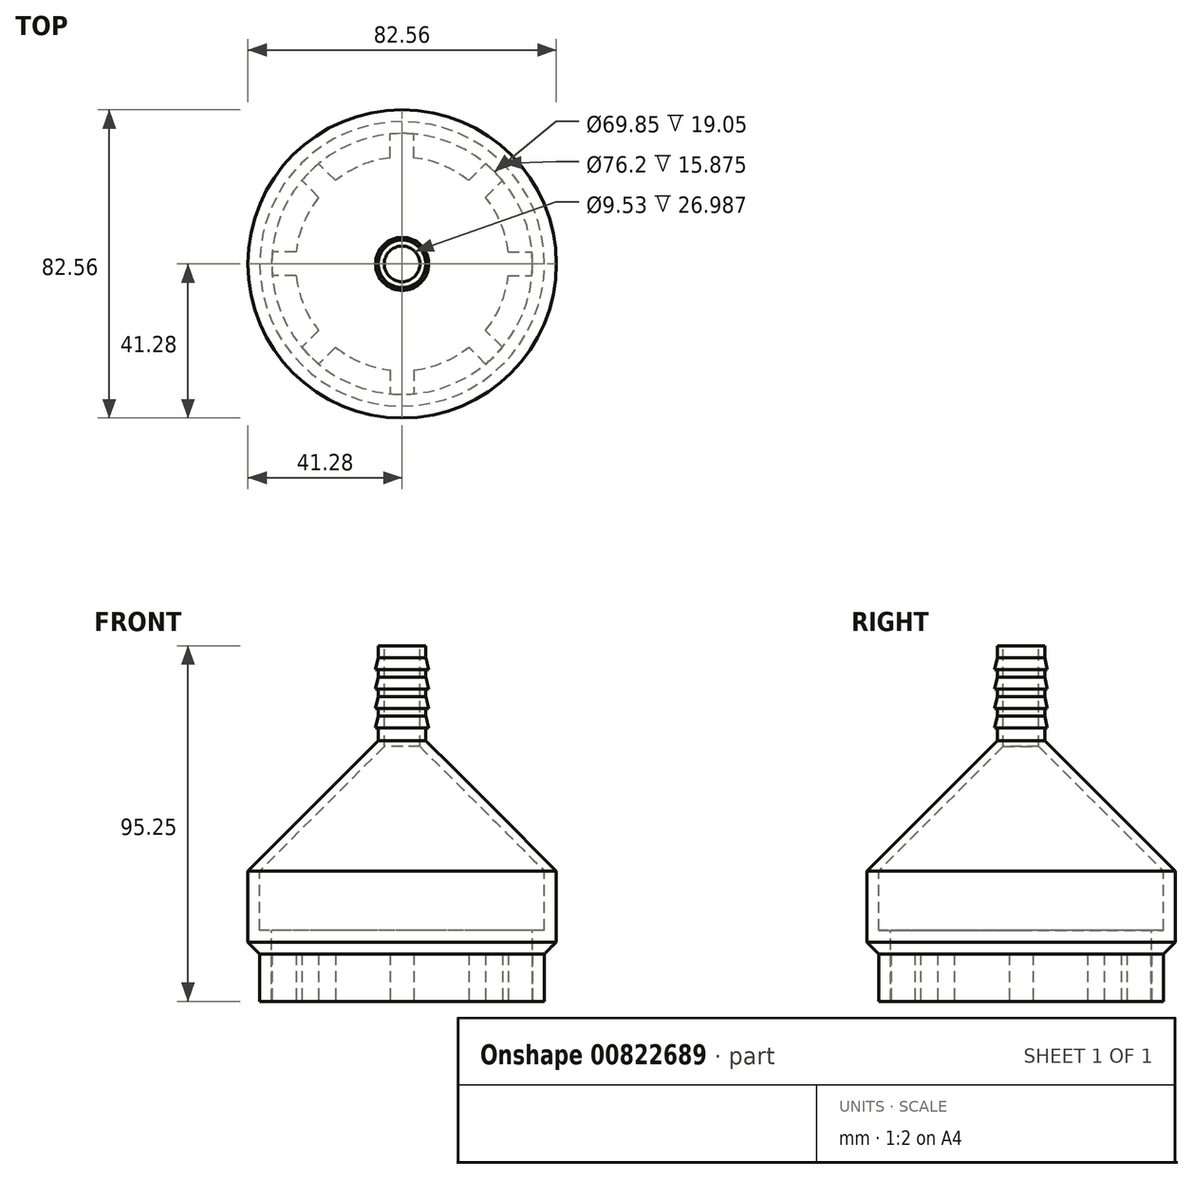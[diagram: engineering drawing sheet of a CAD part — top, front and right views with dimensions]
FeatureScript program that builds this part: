
annotation { "Feature Type Name" : "Feature", "Feature Type Description" : "" }
export const myFeature = defineFeature(function(context is Context, id is Id, definition is map)
    precondition{}
    {
        {
            var Q0;
            Q0=qCreatedBy(makeId("Front.planeOp"),FACE);
            var sketch = newSketch(context, id + "F0", { "sketchPlane" : qUnion([Q0])});
            skLineSegment(sketch, "E0", {"start": v(0, 0) * mm, "end": v(0, 101.6) * mm});
            skLineSegment(sketch, "E1", {"start": v(-34.93, 0) * mm, "end": v(0, 0) * mm});
            skLineSegment(sketch, "E2", {"start": v(-34.93, 0) * mm, "end": v(-38.1, 0) * mm});
            skLineSegment(sketch, "E3", {"start": v(-38.1, 0) * mm, "end": v(-38.1, 12.7) * mm});
            skLineSegment(sketch, "E4", {"start": v(-38.1, 12.7) * mm, "end": v(-41.27, 15.87) * mm});
            skLineSegment(sketch, "E5", {"start": v(-41.27, 15.87) * mm, "end": v(-41.27, 34.92) * mm});
            skLineSegment(sketch, "E6", {"start": v(-41.27, 34.92) * mm, "end": v(-6.35, 69.85) * mm});
            skLineSegment(sketch, "E7", {"start": v(-34.93, 0) * mm, "end": v(-34.93, 19.05) * mm});
            skLineSegment(sketch, "E8", {"start": v(-34.93, 19.05) * mm, "end": v(-38.1, 19.05) * mm});
            skLineSegment(sketch, "E9", {"start": v(-38.1, 19.05) * mm, "end": v(-38.1, 34.92) * mm});
            skLineSegment(sketch, "E10", {"start": v(-38.1, 34.92) * mm, "end": v(-4.76, 68.26) * mm});
            skLineSegment(sketch, "E11", {"start": v(-6.35, 95.25) * mm, "end": v(-4.76, 95.25) * mm});
            skLineSegment(sketch, "E12", {"start": v(-4.76, 95.25) * mm, "end": v(-4.76, 68.26) * mm});
            skLineSegment(sketch, "E13", {"start": v(-6.35, 95.25) * mm, "end": v(-6.35, 92.07) * mm});
            skLineSegment(sketch, "E14", {"start": v(-6.35, 92.07) * mm, "end": v(-7.11, 88.9) * mm});
            skLineSegment(sketch, "E15", {"start": v(-7.11, 88.9) * mm, "end": v(-6.35, 88.9) * mm});
            skLineSegment(sketch, "E16", {"start": v(-6.35, 88.9) * mm, "end": v(-6.35, 86.87) * mm});
            skLineSegment(sketch, "E17", {"start": v(-6.35, 86.87) * mm, "end": v(-7.11, 83.7) * mm});
            skLineSegment(sketch, "E18", {"start": v(-7.11, 83.7) * mm, "end": v(-6.35, 83.7) * mm});
            skLineSegment(sketch, "E19", {"start": v(-6.35, 83.7) * mm, "end": v(-6.35, 81.66) * mm});
            skLineSegment(sketch, "E20", {"start": v(-6.35, 81.66) * mm, "end": v(-7.11, 78.49) * mm});
            skLineSegment(sketch, "E21", {"start": v(-7.11, 78.49) * mm, "end": v(-6.35, 78.49) * mm});
            skLineSegment(sketch, "E22", {"start": v(-6.35, 78.49) * mm, "end": v(-6.35, 76.45) * mm});
            skLineSegment(sketch, "E23", {"start": v(-6.35, 76.45) * mm, "end": v(-7.11, 73.28) * mm});
            skLineSegment(sketch, "E24", {"start": v(-7.11, 73.28) * mm, "end": v(-6.35, 73.28) * mm});
            skLineSegment(sketch, "E25", {"start": v(-6.35, 73.28) * mm, "end": v(-6.35, 69.85) * mm});
            skSolve(sketch);
        }
        {
            var Q0;
            Q0=makeQuery(id+"F0.imprint","IMPRINT",FACE,{"disambiguationData":[TD([[makeQuery(id+"F0.imprint","IMPRINT",EDGE,{"derivedFrom":sQuery(id+"F0.wireOp",EDGE,"E2")}),-1.0]])]});
            var Q1;
            Q1=sQuery(id+"F0.wireOp",EDGE,"E0");
            revolve(context, id + "F1", {"surfaceOperationType" : NewSurfaceOperationType.NEW, "entities" : qUnion([Q0]), "axis" : qUnion([Q1]), "revolveType" : RevolveType.FULL, "oppositeDirection" : true});
        }
        {
            var Q0;
            Q0=qCreatedBy(makeId("Top.planeOp"),FACE);
            var sketch = newSketch(context, id + "F2", { "sketchPlane" : qUnion([Q0])});
            skArc(sketch, "E26", {"start": v(-3.17, -34.78) * mm, "mid": v(0, -34.92) * mm, "end": v(3.18, -34.78) * mm});
            skLineSegment(sketch, "E27", {"start": v(-28.4, -3.18) * mm, "end": v(-34.78, -3.18) * mm});
            skLineSegment(sketch, "E28", {"start": v(-3.17, 28.4) * mm, "end": v(-3.17, 34.78) * mm});
            skLineSegment(sketch, "E29", {"start": v(3.17, 28.4) * mm, "end": v(3.17, 34.78) * mm});
            skArc(sketch, "E30", {"start": v(3.17, 34.78) * mm, "mid": v(0, 34.93) * mm, "end": v(-3.17, 34.78) * mm});
            skLineSegment(sketch, "E31", {"start": v(-28.4, 3.18) * mm, "end": v(-34.78, 3.18) * mm});
            skLineSegment(sketch, "E32", {"start": v(28.4, 3.18) * mm, "end": v(34.78, 3.18) * mm});
            skLineSegment(sketch, "E33", {"start": v(28.4, -3.17) * mm, "end": v(34.78, -3.17) * mm});
            skArc(sketch, "E34", {"start": v(34.78, -3.17) * mm, "mid": v(34.92, 0) * mm, "end": v(34.78, 3.18) * mm});
            skPoint(sketch, "E35.orphan", {"position": v(0, 0) * mm});
            skLineSegment(sketch, "E36", {"start": v(-3.17, -28.4) * mm, "end": v(-3.17, -34.78) * mm});
            skLineSegment(sketch, "E37", {"start": v(3.18, -28.4) * mm, "end": v(3.18, -34.78) * mm});
            skArc(sketch, "E38", {"start": v(22.35, -26.84) * mm, "mid": v(24.7, -24.7) * mm, "end": v(26.84, -22.35) * mm});
            skLineSegment(sketch, "E39", {"start": v(22.35, -26.84) * mm, "end": v(17.84, -22.33) * mm});
            skLineSegment(sketch, "E40", {"start": v(26.84, -22.35) * mm, "end": v(22.33, -17.84) * mm});
            skLineSegment(sketch, "E41", {"start": v(-22.33, 17.84) * mm, "end": v(-26.84, 22.35) * mm});
            skLineSegment(sketch, "E42", {"start": v(-17.84, 22.33) * mm, "end": v(-22.35, 26.84) * mm});
            skLineSegment(sketch, "E43", {"start": v(-22.33, -17.84) * mm, "end": v(-26.84, -22.35) * mm});
            skLineSegment(sketch, "E44", {"start": v(-17.84, -22.33) * mm, "end": v(-22.35, -26.84) * mm});
            skArc(sketch, "E45", {"start": v(-26.84, -22.35) * mm, "mid": v(-24.7, -24.7) * mm, "end": v(-22.35, -26.84) * mm});
            skLineSegment(sketch, "E46", {"start": v(17.84, 22.33) * mm, "end": v(22.35, 26.84) * mm});
            skLineSegment(sketch, "E47", {"start": v(22.33, 17.84) * mm, "end": v(26.84, 22.35) * mm});
            skArc(sketch, "E48", {"start": v(26.84, 22.35) * mm, "mid": v(24.7, 24.7) * mm, "end": v(22.35, 26.84) * mm});
            skArc(sketch, "E49", {"start": v(-22.35, 26.84) * mm, "mid": v(-24.68, 24.68) * mm, "end": v(-26.84, 22.35) * mm});
            skArc(sketch, "E50", {"start": v(-17.84, -22.33) * mm, "mid": v(-10.94, -26.4) * mm, "end": v(-3.17, -28.4) * mm});
            skArc(sketch, "E51.trimOffspring", {"start": v(3.18, -28.4) * mm, "mid": v(10.94, -26.4) * mm, "end": v(17.84, -22.33) * mm});
            skArc(sketch, "E52.trimOffspring", {"start": v(22.33, -17.84) * mm, "mid": v(26.4, -10.94) * mm, "end": v(28.4, -3.17) * mm});
            skArc(sketch, "E53.trimOffspring", {"start": v(28.4, 3.18) * mm, "mid": v(26.4, 10.94) * mm, "end": v(22.33, 17.84) * mm});
            skArc(sketch, "E54.trimOffspring", {"start": v(17.84, 22.33) * mm, "mid": v(10.94, 26.4) * mm, "end": v(3.17, 28.4) * mm});
            skArc(sketch, "E55.trimOffspring", {"start": v(-3.17, 28.4) * mm, "mid": v(-10.94, 26.4) * mm, "end": v(-17.84, 22.33) * mm});
            skArc(sketch, "E56.trimOffspring", {"start": v(-22.33, 17.84) * mm, "mid": v(-26.4, 10.94) * mm, "end": v(-28.4, 3.18) * mm});
            skArc(sketch, "E57", {"start": v(-34.78, 3.18) * mm, "mid": v(-34.92, 0) * mm, "end": v(-34.78, -3.18) * mm});
            skArc(sketch, "E58.trimOffspring", {"start": v(-28.4, -3.18) * mm, "mid": v(-26.4, -10.94) * mm, "end": v(-22.33, -17.84) * mm});
            skSolve(sketch);
        }
        {
            var Q0;
            Q0=makeQuery(id+"F2.imprint","IMPRINT",FACE,{"disambiguationData":[TD([[makeQuery(id+"F2.imprint","IMPRINT",EDGE,{"derivedFrom":sQuery(id+"F2.wireOp",EDGE,"E26")}),1.0]])]});
            extrude(context, id + "F3", {"entities" : qUnion([Q0]), "operationType" : NewBodyOperationType.ADD, "depth" : 12.7 * mm, "offsetDistance" : 25.4 * mm});
        }
    });
